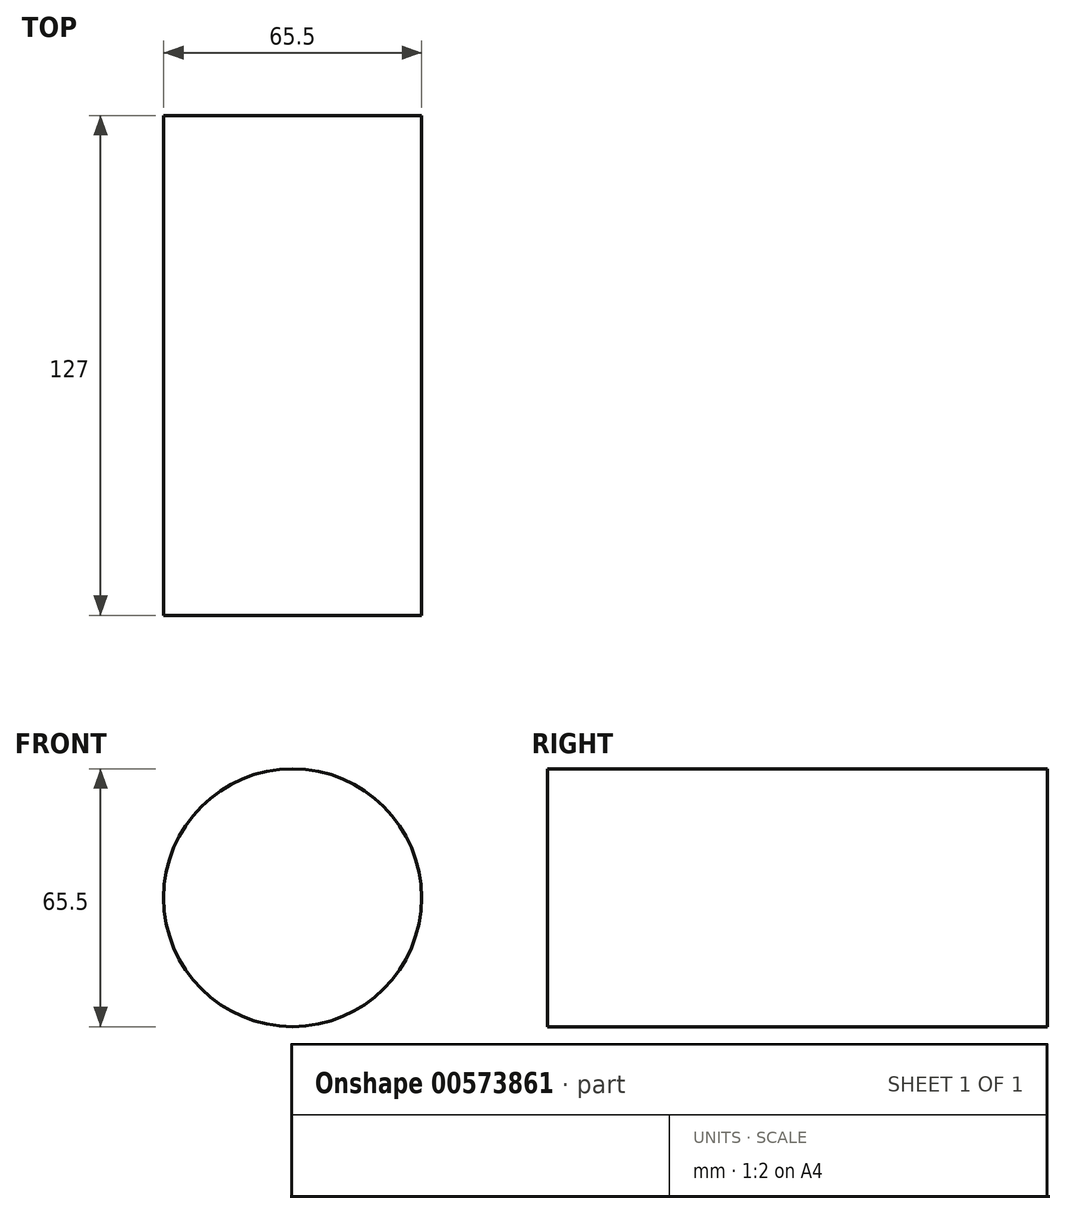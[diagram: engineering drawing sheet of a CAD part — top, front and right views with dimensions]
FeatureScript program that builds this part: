
annotation { "Feature Type Name" : "Feature", "Feature Type Description" : "" }
export const myFeature = defineFeature(function(context is Context, id is Id, definition is map)
    precondition{}
    {
        {
            var Q0;
            Q0=qCreatedBy(makeId("Front.planeOp"),FACE);
            var sketch = newSketch(context, id + "F0", { "sketchPlane" : qUnion([Q0])});
            skCircle(sketch, "E0", {"center": v(0, 0) * mm, "radius": 32.75 * mm});
            skSolve(sketch);
        }
        {
            var Q0;
            Q0=makeQuery(id+"F0.imprint","IMPRINT",FACE,{"disambiguationData":[TD([[makeQuery(id+"F0.imprint","IMPRINT",EDGE,{"derivedFrom":sQuery(id+"F0.wireOp",EDGE,"E0")}),1.0]])]});
            extrude(context, id + "F1", {"entities" : qUnion([Q0]), "depth" : 127 * mm, "offsetDistance" : 25.4 * mm});
        }
    });
